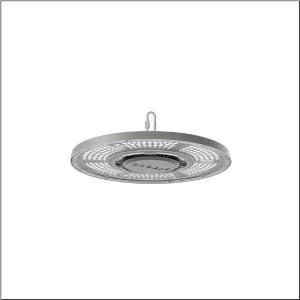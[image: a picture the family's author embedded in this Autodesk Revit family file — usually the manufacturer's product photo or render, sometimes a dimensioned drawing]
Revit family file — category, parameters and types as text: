
# Revit family: highbay_31-s_51hc41da4fmb
name_source: partatom
category: Lighting Fixtures
units: mm (PartAtom-declared; Revit-internal decimal feet)

## family parameters
Cut with Voids When Loaded = No
Host = Face
Light Source = No
Part Type = Normal
Room Calculation Point = No
Round Connector Dimension = Use Diameter
Shared = No

## types (1)
- Highbay 31-S (1 x LED, 14000 lm, 94 W, 4000K)
    Apparent Load = 94 VA
    CIE Flux Codes = 94 98 100 100 100
    Color Rendering = 80
    Color Temperature = 4000K
    Default Elevation = 1800 mm
    Description = Highbay 31-S, LED high bay luminaire, primary light control with lens, of PC, primary optical cover: cover panel, of PC, transparent, light emission: direct distribution, primary light characteristic: rotationally symmetric, installation type: suspended mounting, surface-mounted, LED, rated luminous flux: 14.000lm, luminous efficacy: 150lm/W, light colour: 840, colour temperature: 4000K, control gear: ECG DALI, with cable, 5x 1.0mm², free wire ends, mains connection: 220..240V, AC/DC, 0/50..60Hz, cable length: 1,5m, rated input power: 94W, housing, rotationally symmetric, of diecast aluminium, powder-coated, grey aluminium (RAL 9007), with hook on luminaire side, incl. screw, diameter: 339mm, protection rating (complete): IP65, insulation class (complete): insulation class I (protective earthing), certification: CE, ENEC, UKCA, protection symbol: D, impact resistance: IK08, permissible operating ambient temperature: -30..+45°C, standard: EN 60598-2-22, EN 60598, corresponds to IFS (International Featured Standards) requirements for safety and quality in the food industry, packaging unit: 1 piece
    Height = 141 mm
    Lamp = 1 x LED
    Lamp Light Flux = 14000 lm
    Lamp Power = 94 W
    Lamp count = 1
    Length = 339 mm
    Luminous efficacy = 149 lm/W
    Manufacturer = Siteco
    ModVariant = No
    Model = 51HC41DA4FMB
    Mounting Place = Ceiling
    Mounting Type = Pendant
    Number of Poles = 1
    OnlyDefault = Yes
    Power Factor = 1
    Product Name = Highbay 31-S
    Product group = LED high bay luminaire
    ProductGroupID = 903
    Protection Class = Protection class I
    Protection Degree = IP 65
    RLX_Detail_Level = 1
    RLX_Emergency_Light_Flux = 0 lm
    RLX_Emergency_Type = 0
    RLX_Emergency_Type_DB = No
    RlxData = <blob elided: 107537 chars, md5=dc9123a6>
    Socket = socket
    Standby Power = 0 W
    System Light Flux = 14000 lm
    System Power = 94 W
    Type Comments = Product without accessories
    Type Image = l_1007237.jpg
    URL = http://relux.com
    VarID = ---
    Voltage = 0 V
    Weight = 0.00 kg
    Width = 0 mm  [stored 0 ft]

note: [stored X ft] marks values corroborated as IEEE doubles in the binary element streams (Revit-internal decimal feet)

## geometry (parser evidence)
native form markers: Blend x4, Sweep x10
no freeform markers — native parametric forms only
